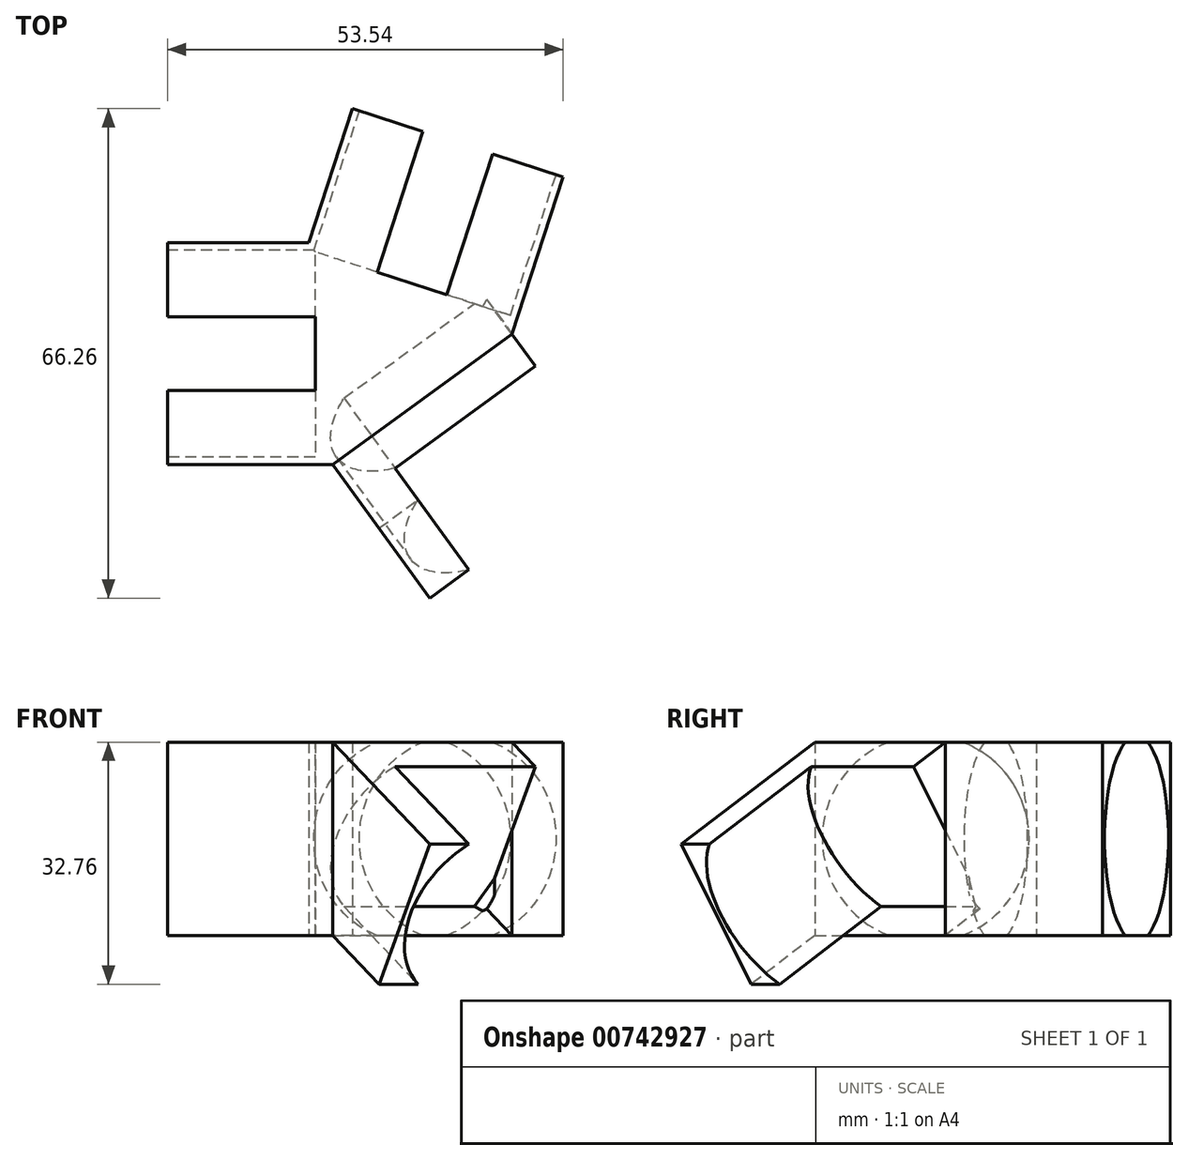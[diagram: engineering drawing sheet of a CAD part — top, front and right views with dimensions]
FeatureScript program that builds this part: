
annotation { "Feature Type Name" : "Feature", "Feature Type Description" : "" }
export const myFeature = defineFeature(function(context is Context, id is Id, definition is map)
    precondition{}
    {
        {
            var Q0;
            Q0=qCreatedBy(makeId("Top.planeOp"),FACE);
            var sketch = newSketch(context, id + "F0", { "sketchPlane" : qUnion([Q0])});
            skLineSegment(sketch, "E0.0", {"start": v(0, 0) * mm, "end": v(-30, 0) * mm});
            skLineSegment(sketch, "E0.4", {"start": v(9.27, 28.53) * mm, "end": v(0, 0) * mm});
            skLineSegment(sketch, "E1", {"start": v(0, 0) * mm, "end": v(17.63, -24.27) * mm});
            skLineSegment(sketch, "E2.0", {"start": v(-12.14, -8.82) * mm, "end": v(5.5, -33.09) * mm});
            skLineSegment(sketch, "E3.0", {"start": v(12.14, 8.82) * mm, "end": v(29.77, -15.45) * mm});
            skLineSegment(sketch, "E4.0", {"start": v(0, 15) * mm, "end": v(-30, 15) * mm});
            skLineSegment(sketch, "E5.0", {"start": v(0, -15) * mm, "end": v(-30, -15) * mm});
            skLineSegment(sketch, "E6.0", {"start": v(-5, 33.17) * mm, "end": v(-14.27, 4.64) * mm});
            skLineSegment(sketch, "E7.0", {"start": v(23.54, 23.9) * mm, "end": v(14.27, -4.64) * mm});
            skLineSegment(sketch, "E8", {"start": v(29.77, -15.45) * mm, "end": v(5.5, -33.09) * mm});
            skLineSegment(sketch, "E9", {"start": v(-30, -15) * mm, "end": v(-30, 15) * mm});
            skLineSegment(sketch, "E10", {"start": v(23.54, 23.9) * mm, "end": v(-5, 33.17) * mm});
            skSolve(sketch);
        }
        {
            var Q0;
            {var subQ8=sQuery(id+"F0.wireOp",EDGE,"E0.0");Q0=makeQuery(id+"F0.imprint","IMPRINT",FACE,{"disambiguationData":[TD([[makeQuery(id+"F0.imprint","IMPRINT",EDGE,{"derivedFrom":subQ8}),1.0]])]});}
            var Q1;
            {var subQ8=sQuery(id+"F0.wireOp",EDGE,"E0.4");Q1=makeQuery(id+"F0.imprint","IMPRINT",FACE,{"disambiguationData":[TD([[makeQuery(id+"F0.imprint","IMPRINT",EDGE,{"derivedFrom":subQ8}),1.0]])]});}
            var Q2;
            {var subQ7=sQuery(id+"F0.wireOp",EDGE,"E0.0");Q2=makeQuery(id+"F0.imprint","IMPRINT",FACE,{"disambiguationData":[TD([[makeQuery(id+"F0.imprint","IMPRINT",EDGE,{"derivedFrom":subQ7}),-1.0]])]});}
            extrude(context, id + "F1", {"entities" : qUnion([Q0, Q1, Q2]), "depth" : 40 * mm, "offsetDistance" : 25 * mm});
        }
        {
            var Q0;
            Q0=makeQuery(id+"F1.opExtrude","SWEPT_FACE",FACE,{"disambiguationData":[OSD([sQuery(id+"F0.wireOp",EDGE,"E3.0")])]});
            var sketch = newSketch(context, id + "F2", { "sketchPlane" : qUnion([Q0])});
            skLineSegment(sketch, "E11", {"start": v(-7.64, 40) * mm, "end": v(-30, 26.18) * mm});
            skLineSegment(sketch, "E12", {"start": v(-30, 26.18) * mm, "end": v(-30, 40) * mm});
            skLineSegment(sketch, "E13", {"start": v(-30, 40) * mm, "end": v(-7.64, 40) * mm});
            skPoint(sketch, "E14", {"position": v(-7.64, 40) * mm});
            skLineSegment(sketch, "E15", {"start": v(-18.3, 7.24) * mm, "end": v(-7.64, 13.82) * mm});
            skLineSegment(sketch, "E16", {"start": v(-30, 26.18) * mm, "end": v(-18.3, 7.24) * mm});
            skPoint(sketch, "E17.orphan", {"position": v(-30, 0) * mm});
            skSolve(sketch);
        }
        {
            var Q0;
            Q0=makeQuery(id+"F2.imprint","IMPRINT",FACE,{"disambiguationData":[TD([[makeQuery(id+"F2.imprint","IMPRINT",EDGE,{"derivedFrom":sQuery(id+"F2.wireOp",EDGE,"E11")}),-1.0]])]});
            var Q1;
            {var subQ4=sQuery(id+"F2.wireOp",EDGE,"E15");Q1=makeQuery(id+"F2.imprint","IMPRINT",FACE,{"disambiguationData":[TD([[makeQuery(id+"F2.imprint","IMPRINT",EDGE,{"derivedFrom":subQ4}),-1.0]])]});}
            extrude(context, id + "F3", {"entities" : qUnion([Q0, Q1]), "operationType" : NewBodyOperationType.REMOVE, "endBound" : BoundingType.UP_TO_NEXT, "oppositeDirection" : true, "depth" : 25 * mm, "offsetDistance" : 25 * mm});
        }
        {
            var Q0;
            Q0=makeQuery(id+"F1.opExtrude","CAP_FACE",FACE,{"disambiguationData":[OSD([sQuery(id+"F0.wireOp",EDGE,"E2.0"),sQuery(id+"F0.wireOp",EDGE,"E3.0"),sQuery(id+"F0.wireOp",EDGE,"E4.0"),sQuery(id+"F0.wireOp",EDGE,"E5.0"),sQuery(id+"F0.wireOp",EDGE,"E6.0"),sQuery(id+"F0.wireOp",EDGE,"E7.0"),sQuery(id+"F0.wireOp",EDGE,"E8"),sQuery(id+"F0.wireOp",EDGE,"E9"),sQuery(id+"F0.wireOp",EDGE,"E10")])],"isStart":true});
            var Q1;
            Q1=makeQuery(id+"F3.boolean.opBoolean","COPY",VERTEX,{"derivedFrom":makeQuery(id+"F3.opExtrude","CAP_VERTEX",VERTEX,{"disambiguationData":[OSD([sQuery(id+"F0.wireOp",EDGE,"E3.0"),sQuery(id+"F0.wireOp",EDGE,"E7.0"),sQuery(id+"F2.wireOp",EDGE,"E15")])],"isStart":true})});
            extrude(context, id + "F4", {"entities" : qUnion([Q0]), "operationType" : NewBodyOperationType.REMOVE, "endBound" : BoundingType.UP_TO_VERTEX, "oppositeDirection" : true, "depth" : 25 * mm, "endBoundEntityVertex" : qUnion([Q1]), "offsetDistance" : 25 * mm});
        }
        {
            var Q0;
            Q0=makeQuery(id+"F3.boolean.opBoolean","COPY",FACE,{"derivedFrom":makeQuery(id+"F3.opExtrude","SWEPT_FACE",FACE,{"disambiguationData":[OSD([sQuery(id+"F2.wireOp",EDGE,"E16")])]})});
            var sketch = newSketch(context, id + "F5", { "sketchPlane" : qUnion([Q0])});
            skLineSegment(sketch, "E18", {"start": v(-0.44, 40.9) * mm, "end": v(19.64, 9.38) * mm, "construction": true});
            skCircle(sketch, "E19", {"center": v(9.6, 25.14) * mm, "radius": 14 * mm});
            skSolve(sketch);
        }
        {
            var Q0;
            {var subQ0=sQuery(id+"F5.wireOp",EDGE,"E19");var subQ1=sQuery(id+"F2.wireOp",EDGE,"E16");var subQ8=makeQuery(id+"F3.boolean.opBoolean","COPY",EDGE,{"derivedFrom":makeQuery(id+"F3.opExtrude","SWEPT_EDGE",EDGE,{"disambiguationData":[OSD([sQuery(id+"F2.wireOp",EDGE,"E15"),subQ1])]})});var subQ9=makeQuery(id+"F5.imprint","INTERSECT",VERTEX,{"disambiguationData":[OD(0.0)],"derivedFrom":[subQ8,subQ0]});Q0=makeQuery(id+"F5.imprint","IMPRINT",FACE,{"disambiguationData":[TD([[makeQuery(id+"F5.imprint","IMPRINT",EDGE,{"disambiguationData":[TD([[subQ9,-1.0]])],"derivedFrom":subQ8}),1.0]])]});}
            var Q1;
            {var subQ0=sQuery(id+"F5.wireOp",EDGE,"E19");var subQ1=makeQuery(id+"F3.boolean.opBoolean","COPY",EDGE,{"derivedFrom":makeQuery(id+"F3.opExtrude","SWEPT_EDGE",EDGE,{"disambiguationData":[OSD([sQuery(id+"F2.wireOp",EDGE,"E15"),sQuery(id+"F2.wireOp",EDGE,"E16")])]})});var subQ2=makeQuery(id+"F5.imprint","INTERSECT",VERTEX,{"disambiguationData":[OD(0.0)],"derivedFrom":[subQ1,subQ0]});Q1=makeQuery(id+"F5.imprint","IMPRINT",FACE,{"disambiguationData":[TD([[makeQuery(id+"F5.imprint","IMPRINT",EDGE,{"disambiguationData":[TD([[subQ2,-1.0]])],"derivedFrom":subQ0}),1.0]])]});}
            extrude(context, id + "F6", {"entities" : qUnion([Q0, Q1]), "operationType" : NewBodyOperationType.REMOVE, "oppositeDirection" : true, "depth" : 20 * mm, "offsetDistance" : 25 * mm});
        }
        {
            var Q0;
            Q0=makeQuery(id+"F1.opExtrude","SWEPT_FACE",FACE,{"disambiguationData":[OSD([sQuery(id+"F0.wireOp",EDGE,"E10")])]});
            var sketch = newSketch(context, id + "F7", { "sketchPlane" : qUnion([Q0])});
            skLineSegment(sketch, "E20", {"start": v(-15, 40) * mm, "end": v(15, 13.82) * mm, "construction": true});
            skCircle(sketch, "E21", {"center": v(0, 26.9) * mm, "radius": 14 * mm});
            skSolve(sketch);
        }
        {
            var Q0;
            Q0=qSketchRegion(id+"F7",true);
            extrude(context, id + "F8", {"entities" : qUnion([Q0]), "operationType" : NewBodyOperationType.REMOVE, "oppositeDirection" : true, "depth" : 20 * mm, "offsetDistance" : 25 * mm});
        }
        {
            var Q0;
            Q0=makeQuery(id+"F1.opExtrude","SWEPT_FACE",FACE,{"disambiguationData":[OSD([sQuery(id+"F0.wireOp",EDGE,"E9")])]});
            var sketch = newSketch(context, id + "F9", { "sketchPlane" : qUnion([Q0])});
            skLineSegment(sketch, "E22", {"start": v(-15, 40) * mm, "end": v(15, 13.82) * mm, "construction": true});
            skCircle(sketch, "E23", {"center": v(0, 26.9) * mm, "radius": 14 * mm});
            skSolve(sketch);
        }
        {
            var Q0;
            Q0=qSketchRegion(id+"F9",true);
            extrude(context, id + "F10", {"entities" : qUnion([Q0]), "operationType" : NewBodyOperationType.REMOVE, "oppositeDirection" : true, "depth" : 20 * mm, "offsetDistance" : 25 * mm});
        }
    });
